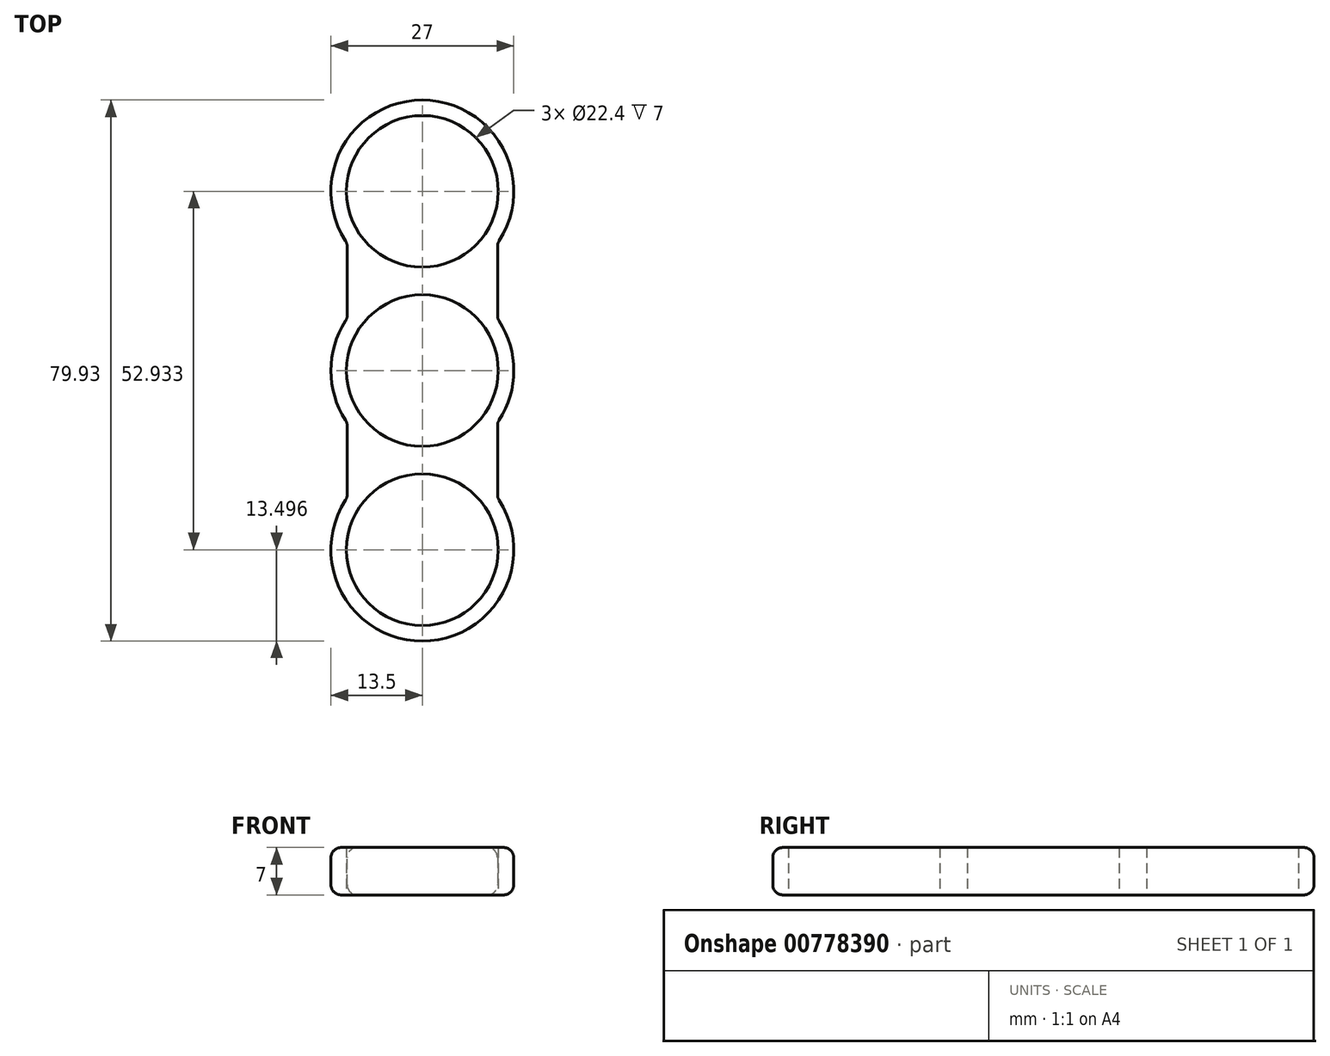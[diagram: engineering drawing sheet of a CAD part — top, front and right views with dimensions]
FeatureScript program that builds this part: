
annotation { "Feature Type Name" : "Feature", "Feature Type Description" : "" }
export const myFeature = defineFeature(function(context is Context, id is Id, definition is map)
    precondition{}
    {
        {
            var Q0;
            Q0=qCreatedBy(makeId("Top.planeOp"),FACE);
            var sketch = newSketch(context, id + "F0", { "sketchPlane" : qUnion([Q0])});
            skCircle(sketch, "E0", {"center": v(0, 0) * mm, "radius": 11.2 * mm});
            skArc(sketch, "E1", {"start": v(11.1, -7.69) * mm, "mid": v(13.5, 0) * mm, "end": v(11.1, 7.69) * mm});
            skCircle(sketch, "E2", {"center": v(0, 26.47) * mm, "radius": 11.2 * mm});
            skArc(sketch, "E3", {"start": v(11.1, 18.78) * mm, "mid": v(0, 39.97) * mm, "end": v(-11.1, 18.78) * mm});
            skCircle(sketch, "E4.1.0", {"center": v(0, -26.46) * mm, "radius": 11.2 * mm});
            skArc(sketch, "E5", {"start": v(-11.1, -18.78) * mm, "mid": v(0, -39.96) * mm, "end": v(11.1, -18.78) * mm});
            skLineSegment(sketch, "E6", {"start": v(-11.1, 18.78) * mm, "end": v(-11.1, 7.69) * mm});
            skLineSegment(sketch, "E7", {"start": v(11.1, 18.78) * mm, "end": v(11.1, 7.69) * mm});
            skLineSegment(sketch, "E8", {"start": v(-11.1, -7.69) * mm, "end": v(-11.1, -18.78) * mm});
            skLineSegment(sketch, "E9", {"start": v(11.1, -7.69) * mm, "end": v(11.1, -18.78) * mm});
            skArc(sketch, "E10.trimOffspring", {"start": v(-11.1, 7.69) * mm, "mid": v(-13.5, 0) * mm, "end": v(-11.1, -7.69) * mm});
            skSolve(sketch);
        }
        {
            var Q0;
            Q0=makeQuery(id+"F0.imprint","IMPRINT",FACE,{"disambiguationData":[TD([[makeQuery(id+"F0.imprint","IMPRINT",EDGE,{"derivedFrom":sQuery(id+"F0.wireOp",EDGE,"E0")}),-1.0]])]});
            extrude(context, id + "F1", {"entities" : qUnion([Q0]), "depth" : 7 * mm, "offsetDistance" : 25 * mm});
        }
        {
            var Q0;
            Q0=makeQuery(id+"F1.opExtrude","SWEPT_FACE",FACE,{"disambiguationData":[OSD([sQuery(id+"F0.wireOp",EDGE,"E3")])]});
            var Q1;
            Q1=makeQuery(id+"F1.opExtrude","SWEPT_FACE",FACE,{"disambiguationData":[OSD([sQuery(id+"F0.wireOp",EDGE,"E7")])]});
            var Q2;
            Q2=makeQuery(id+"F1.opExtrude","SWEPT_FACE",FACE,{"disambiguationData":[OSD([sQuery(id+"F0.wireOp",EDGE,"E1")])]});
            var Q3;
            Q3=makeQuery(id+"F1.opExtrude","SWEPT_FACE",FACE,{"disambiguationData":[OSD([sQuery(id+"F0.wireOp",EDGE,"E9")])]});
            var Q4;
            Q4=makeQuery(id+"F1.opExtrude","SWEPT_FACE",FACE,{"disambiguationData":[OSD([sQuery(id+"F0.wireOp",EDGE,"E5")])]});
            var Q5;
            Q5=makeQuery(id+"F1.opExtrude","SWEPT_FACE",FACE,{"disambiguationData":[OSD([sQuery(id+"F0.wireOp",EDGE,"E6")])]});
            var Q6;
            Q6=makeQuery(id+"F1.opExtrude","CAP_EDGE",EDGE,{"disambiguationData":[OSD([sQuery(id+"F0.wireOp",EDGE,"E10.trimOffspring")])],"isStart":true});
            var Q7;
            Q7=makeQuery(id+"F1.opExtrude","SWEPT_FACE",FACE,{"disambiguationData":[OSD([sQuery(id+"F0.wireOp",EDGE,"E8")])]});
            var Q8;
            Q8=makeQuery(id+"F1.opExtrude","CAP_EDGE",EDGE,{"disambiguationData":[OSD([sQuery(id+"F0.wireOp",EDGE,"E10.trimOffspring")])],"isStart":false});
            fillet(context, id + "F2", {"entities" : qUnion([Q0, Q1, Q2, Q3, Q4, Q5, Q6, Q7, Q8]), "radius" : 1.5 * mm, "tangentPropagation" : true, "allowEdgeOverflow" : false});
        }
    });
